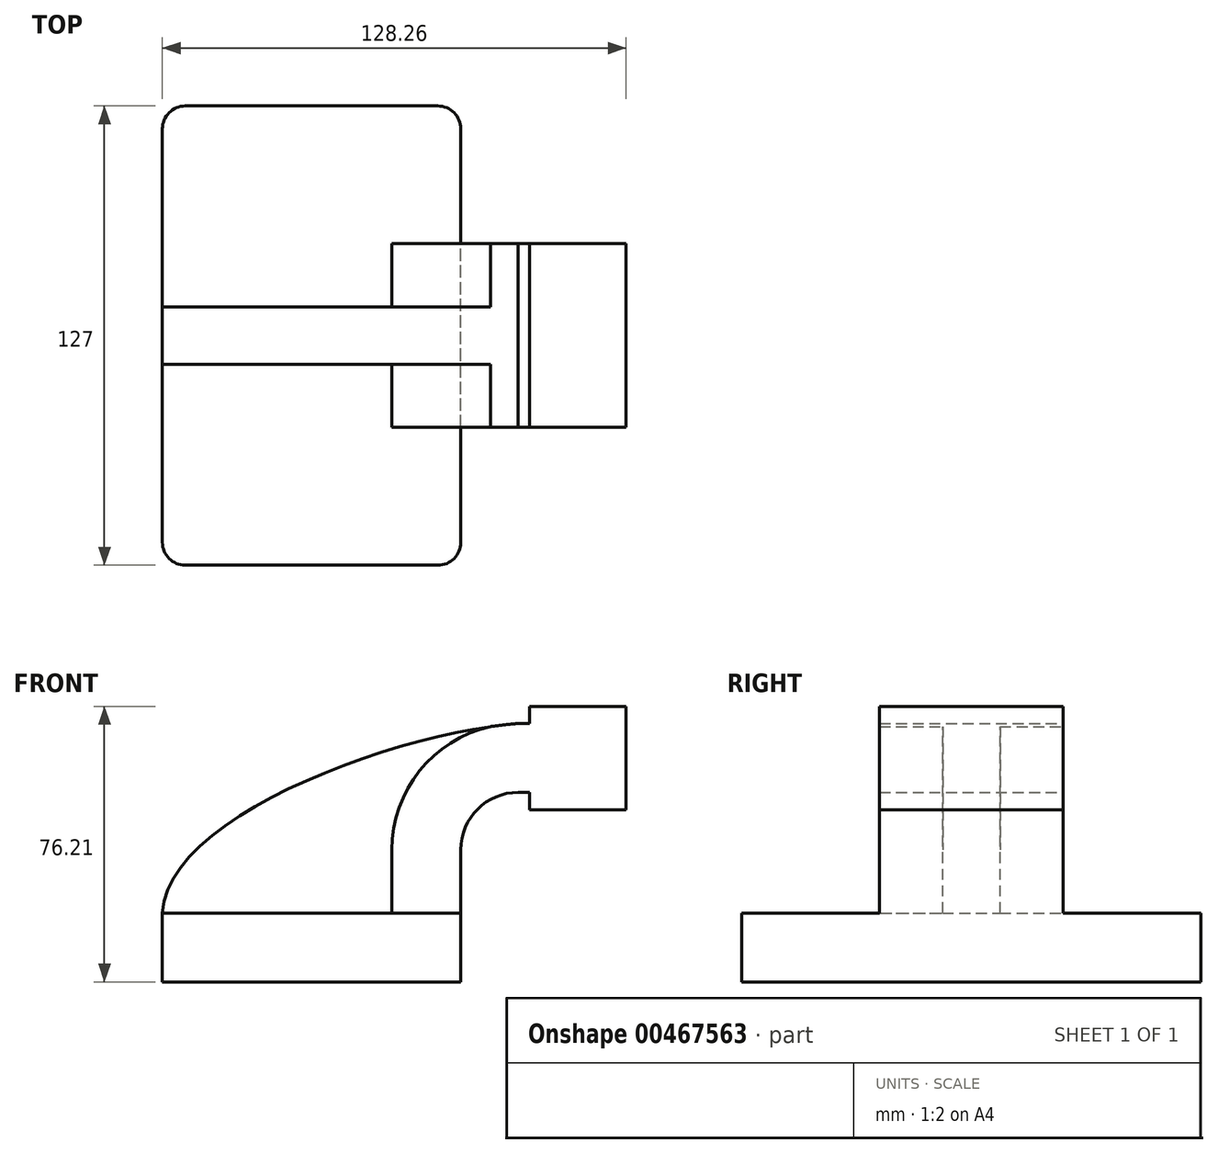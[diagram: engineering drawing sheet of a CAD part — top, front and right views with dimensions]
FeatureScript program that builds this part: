
annotation { "Feature Type Name" : "Feature", "Feature Type Description" : "" }
export const myFeature = defineFeature(function(context is Context, id is Id, definition is map)
    precondition{}
    {
        {
            var Q0;
            Q0=qCreatedBy(makeId("Front.planeOp"),FACE);
            var sketch = newSketch(context, id + "F0", { "sketchPlane" : qUnion([Q0])});
            skLineSegment(sketch, "E0.bottom", {"start": v(-41.28, 9.52) * mm, "end": v(41.28, 9.53) * mm});
            skLineSegment(sketch, "E0.top", {"start": v(-41.28, -9.53) * mm, "end": v(41.28, -9.53) * mm});
            skLineSegment(sketch, "E0.left", {"start": v(-41.28, 9.52) * mm, "end": v(-41.28, -9.53) * mm});
            skLineSegment(sketch, "E0.right", {"start": v(41.28, 9.53) * mm, "end": v(41.28, -9.52) * mm});
            skPoint(sketch, "E0.middle", {"position": v(0, 0) * mm});
            skPoint(sketch, "E1.middle", {"position": v(-41.28, 9.52) * mm});
            skLineSegment(sketch, "E2.bottom", {"start": v(60.32, 66.68) * mm, "end": v(111.12, 66.68) * mm});
            skLineSegment(sketch, "E2.top", {"start": v(60.32, 38.1) * mm, "end": v(111.12, 38.1) * mm});
            skLineSegment(sketch, "E2.left", {"start": v(60.32, 66.68) * mm, "end": v(60.32, 38.1) * mm});
            skLineSegment(sketch, "E2.right", {"start": v(111.12, 66.68) * mm, "end": v(111.12, 38.1) * mm});
            skPoint(sketch, "E2.middle", {"position": v(85.72, 52.39) * mm});
            skLineSegment(sketch, "E3", {"start": v(41.27, 9.53) * mm, "end": v(41.27, 27) * mm});
            skArc(sketch, "E4", {"start": v(41.27, 27) * mm, "mid": v(45.92, 38.23) * mm, "end": v(57.15, 42.88) * mm});
            skLineSegment(sketch, "E5", {"start": v(57.15, 42.88) * mm, "end": v(86.98, 42.88) * mm});
            skLineSegment(sketch, "E6.0", {"start": v(57.15, 61.93) * mm, "end": v(86.98, 61.93) * mm});
            skArc(sketch, "E6.1", {"start": v(22.22, 27) * mm, "mid": v(32.45, 51.7) * mm, "end": v(57.15, 61.93) * mm});
            skLineSegment(sketch, "E6.2", {"start": v(22.22, 9.53) * mm, "end": v(22.22, 27) * mm});
            skLineSegment(sketch, "E7", {"start": v(86.98, 66.68) * mm, "end": v(86.98, 38.1) * mm});
            skFitSpline(sketch, "E8", {"points": [v(-41.28, 9.52) * mm, v(57.15, 61.93) * mm], "startDerivative": vector(3.45, 79.76) * mm, "endDerivative": vector(103.24, 7.9) * mm});
            skSolve(sketch);
        }
        {
            var Q0;
            Q0=makeQuery(id+"F0.imprint","IMPRINT",FACE,{"disambiguationData":[TD([[makeQuery(id+"F0.imprint","IMPRINT",EDGE,{"derivedFrom":sQuery(id+"F0.wireOp",EDGE,"E0.top")}),1.0]])]});
            extrude(context, id + "F1", {"entities" : qUnion([Q0]), "endBound" : BoundingType.SYMMETRIC, "depth" : 127 * mm});
        }
        {
            var Q0;
            {var subQ1=sQuery(id+"F0.wireOp",EDGE,"E3");Q0=makeQuery(id+"F0.imprint","IMPRINT",FACE,{"disambiguationData":[TD([[makeQuery(id+"F0.imprint","IMPRINT",EDGE,{"derivedFrom":subQ1}),1.0]])]});}
            extrude(context, id + "F2", {"entities" : qUnion([Q0]), "operationType" : NewBodyOperationType.ADD, "endBound" : BoundingType.SYMMETRIC, "depth" : 50.8 * mm});
        }
        {
            var Q0;
            {var subQ3=sQuery(id+"F0.wireOp",EDGE,"E6.2");Q0=makeQuery(id+"F0.imprint","IMPRINT",FACE,{"disambiguationData":[TD([[makeQuery(id+"F0.imprint","IMPRINT",EDGE,{"derivedFrom":subQ3}),1.0]])]});}
            extrude(context, id + "F3", {"entities" : qUnion([Q0]), "operationType" : NewBodyOperationType.ADD, "endBound" : BoundingType.SYMMETRIC, "depth" : 15.88 * mm});
        }
        {
            var Q0;
            {var subQ0=sQuery(id+"F0.wireOp",EDGE,"E6.0");var subQ1=sQuery(id+"F0.wireOp",EDGE,"E2.left");var subQ2=makeQuery(id+"F0.imprint","INTERSECT",VERTEX,{"derivedFrom":[subQ1,subQ0]});Q0=makeQuery(id+"F0.imprint","IMPRINT",FACE,{"disambiguationData":[TD([[makeQuery(id+"F0.imprint","IMPRINT",EDGE,{"disambiguationData":[TD([[subQ2,-1.0]])],"derivedFrom":subQ1}),1.0]])]});}
            extrude(context, id + "F4", {"entities" : qUnion([Q0]), "operationType" : NewBodyOperationType.ADD, "endBound" : BoundingType.SYMMETRIC, "depth" : 50.8 * mm});
        }
        {
            var Q0;
            {var subQ0=sQuery(id+"F0.wireOp",EDGE,"E2.left");var subQ1=sQuery(id+"F0.wireOp",EDGE,"E2.bottom");var subQ2=makeQuery(id+"F0.imprint","INTERSECT",VERTEX,{"derivedFrom":[subQ1,subQ0]});Q0=makeQuery(id+"F0.imprint","IMPRINT",FACE,{"disambiguationData":[TD([[makeQuery(id+"F0.imprint","IMPRINT",EDGE,{"disambiguationData":[TD([[subQ2,-1.0]])],"derivedFrom":subQ1}),-1.0]])]});}
            extrude(context, id + "F5", {"entities" : qUnion([Q0]), "operationType" : NewBodyOperationType.ADD, "endBound" : BoundingType.SYMMETRIC, "depth" : 50.8 * mm});
        }
        {
            var Q0;
            {var subQ0=sQuery(id+"F0.wireOp",EDGE,"E2.left");var subQ1=sQuery(id+"F0.wireOp",EDGE,"E2.top");var subQ2=makeQuery(id+"F0.imprint","INTERSECT",VERTEX,{"derivedFrom":[subQ1,subQ0]});Q0=makeQuery(id+"F0.imprint","IMPRINT",FACE,{"disambiguationData":[TD([[makeQuery(id+"F0.imprint","IMPRINT",EDGE,{"disambiguationData":[TD([[subQ2,-1.0]])],"derivedFrom":subQ1}),1.0]])]});}
            extrude(context, id + "F6", {"entities" : qUnion([Q0]), "operationType" : NewBodyOperationType.ADD, "endBound" : BoundingType.SYMMETRIC, "depth" : 50.8 * mm});
        }
        {
            var Q0;
            Q0=makeQuery(id+"F1.opExtrude","CAP_EDGE",EDGE,{"disambiguationData":[OSD([sQuery(id+"F0.wireOp",EDGE,"E0.left")])],"isStart":false});
            var Q1;
            Q1=makeQuery(id+"F1.opExtrude","CAP_EDGE",EDGE,{"disambiguationData":[OSD([sQuery(id+"F0.wireOp",EDGE,"E0.right")])],"isStart":false});
            var Q2;
            Q2=makeQuery(id+"F1.opExtrude","CAP_EDGE",EDGE,{"disambiguationData":[OSD([sQuery(id+"F0.wireOp",EDGE,"E0.right")])],"isStart":true});
            var Q3;
            Q3=makeQuery(id+"F1.opExtrude","CAP_EDGE",EDGE,{"disambiguationData":[OSD([sQuery(id+"F0.wireOp",EDGE,"E0.left")])],"isStart":true});
            fillet(context, id + "F7", {"entities" : qUnion([Q0, Q1, Q2, Q3]), "radius" : 6.35 * mm, "tangentPropagation" : true, "allowEdgeOverflow" : false});
        }
    });
